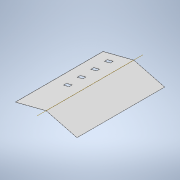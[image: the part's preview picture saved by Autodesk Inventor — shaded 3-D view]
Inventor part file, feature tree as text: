
AUTODESK INVENTOR PART (.ipt)
format: ipt  version: 2022.1 (Build 261234000, 234)  size: 132,608 bytes
history: native  units: in
note: dims shown in document units (in); Inventor stores cm internally (conversion verified against a paired STEP export)
features: other x2, sketch x2, extrude x2
ambient origin geometry x8: Origin, YZ Plane, XZ Plane, XY Plane, X Axis, Y Axis, Z Axis, Center Point
bodies: Body1 (feature_tree)
feature tree (6):
  other  "southPlaneOfRoof"
  other  "norhtPlaneOfRoof"
  sketch  "Sketch3"  dims[d7=0.0992in d8=-0.0992in]
  sketch  "Sketch4"  dims[d9=768.0in d10=279.0in d11=278.0in d12=279.0in d13=768.0in d14=279.0in d15=26.0in d16=51.0in d17=71.0in d18=94.0in d19=93.5in d20=94.0in d21=114.5in d22=114.0in d23=113.0in d24=114.0in d25=1.0in d26=0.0in d27=1.0in d28=0.0in]
  extrude  "Extrusion2"  [1 undecoded]
  extrude  "Extrusion3"  Depth=279.0in
note: 1 required parameter value undecoded (feature->parameter linkage not recoverable at this tier; creation-order binding heuristic only, values carry confidence <= 0.55)
